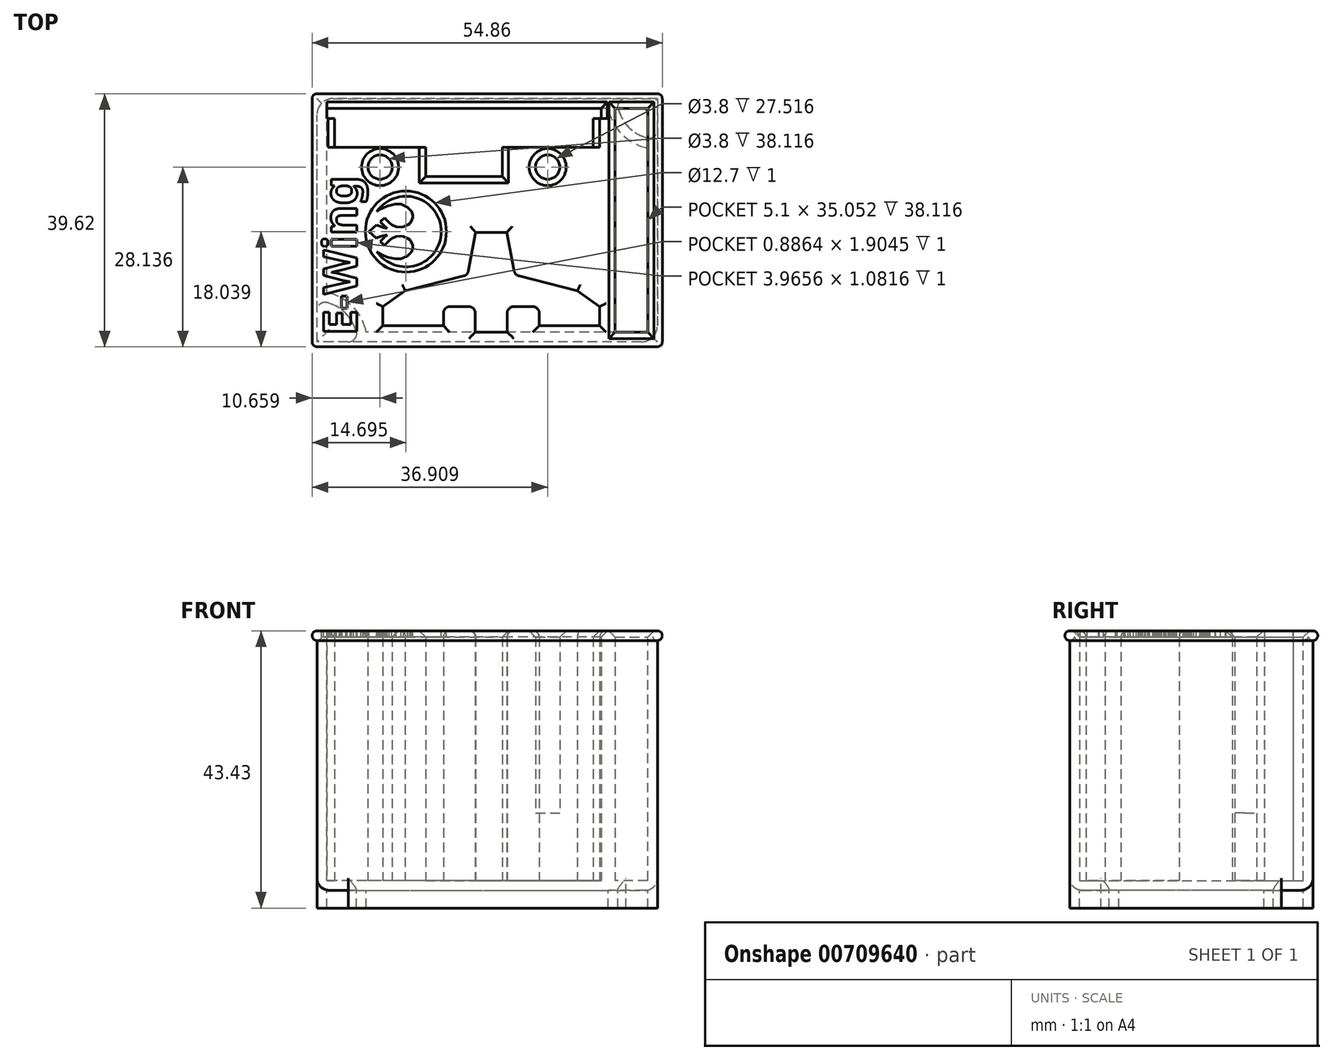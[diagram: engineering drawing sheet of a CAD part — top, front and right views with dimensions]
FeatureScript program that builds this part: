
annotation { "Feature Type Name" : "Feature", "Feature Type Description" : "" }
export const myFeature = defineFeature(function(context is Context, id is Id, definition is map)
    precondition{}
    {
        {
            var Q0;
            Q0=qCreatedBy(makeId("Front.planeOp"),FACE);
            var sketch = newSketch(context, id + "F0", { "sketchPlane" : qUnion([Q0])});
            skLineSegment(sketch, "E0.bottom", {"start": v(26.67, -20.32) * mm, "end": v(-26.67, -20.32) * mm});
            skLineSegment(sketch, "E0.top", {"start": v(26.67, 20.32) * mm, "end": v(-26.67, 20.32) * mm});
            skLineSegment(sketch, "E0.left", {"start": v(26.67, -20.32) * mm, "end": v(26.67, 20.32) * mm});
            skLineSegment(sketch, "E0.right", {"start": v(-26.67, -20.32) * mm, "end": v(-26.67, 20.32) * mm});
            skPoint(sketch, "E0.middle", {"position": v(0, 0) * mm});
            skSolve(sketch);
        }
        {
            var Q0;
            Q0=makeQuery(id+"F0.imprint","IMPRINT",FACE,{"disambiguationData":[TD([[makeQuery(id+"F0.imprint","IMPRINT",EDGE,{"derivedFrom":sQuery(id+"F0.wireOp",EDGE,"E0.bottom")}),-1.0]])]});
            extrude(context, id + "F1", {"entities" : qUnion([Q0]), "depth" : 38.1 * mm, "symmetric" : true});
        }
        {
            var Q0;
            Q0=makeQuery(id+"F1.opExtrude","SWEPT_FACE",FACE,{"disambiguationData":[OSD([sQuery(id+"F0.wireOp",EDGE,"E0.top")])]});
            shell(context, id + "F2", {"entities" : qUnion([Q0]), "thickness" : 1.52 * mm});
        }
        {
            var Q0;
            Q0=makeQuery(id+"F1.opExtrude","CAP_FACE",FACE,{"disambiguationData":[OSD([sQuery(id+"F0.wireOp",EDGE,"E0.bottom"),sQuery(id+"F0.wireOp",EDGE,"E0.top"),sQuery(id+"F0.wireOp",EDGE,"E0.left"),sQuery(id+"F0.wireOp",EDGE,"E0.right")])],"isStart":false});
            var sketch = newSketch(context, id + "F3", { "sketchPlane" : qUnion([Q0])});
            skArc(sketch, "E1", {"start": v(-26.67, 20.32) * mm, "mid": v(-27.43, 19.56) * mm, "end": v(-26.67, 18.8) * mm});
            skSolve(sketch);
        }
        {
            var Q0;
            {var subQ0=sQuery(id+"F3.wireOp",EDGE,"E1");Q0=makeQuery(id+"F3.imprint","IMPRINT",FACE,{"disambiguationData":[TD([[makeQuery(id+"F3.imprint","IMPRINT",EDGE,{"derivedFrom":subQ0}),1.0]])]});}
            var Q1;
            Q1=makeQuery(id+"F1.opExtrude","SWEPT_EDGE",EDGE,{"disambiguationData":[OSD([sQuery(id+"F0.wireOp",EDGE,"E0.top"),sQuery(id+"F0.wireOp",EDGE,"E0.right")])]});
            var Q2;
            Q2=makeQuery(id+"F1.opExtrude","CAP_EDGE",EDGE,{"disambiguationData":[OSD([sQuery(id+"F0.wireOp",EDGE,"E0.top")])],"isStart":true});
            var Q3;
            Q3=makeQuery(id+"F1.opExtrude","SWEPT_EDGE",EDGE,{"disambiguationData":[OSD([sQuery(id+"F0.wireOp",EDGE,"E0.top"),sQuery(id+"F0.wireOp",EDGE,"E0.left")])]});
            var Q4;
            Q4=makeQuery(id+"F1.opExtrude","CAP_EDGE",EDGE,{"disambiguationData":[OSD([sQuery(id+"F0.wireOp",EDGE,"E0.top")])],"isStart":false});
            sweep(context, id + "F4", {"operationType" : NewBodyOperationType.ADD, "profiles" : qUnion([Q0]), "path" : qUnion([Q1, Q2, Q3, Q4])});
        }
        {
            var Q0;
            Q0=makeQuery(id+"F1.opExtrude","SWEPT_FACE",FACE,{"disambiguationData":[OSD([sQuery(id+"F0.wireOp",EDGE,"E0.bottom")])]});
            var sketch = newSketch(context, id + "F5", { "sketchPlane" : qUnion([Q0])});
            skLineSegment(sketch, "E2.bottom", {"start": v(26.67, 19.05) * mm, "end": v(21.75, 19.05) * mm});
            skLineSegment(sketch, "E2.left", {"start": v(26.67, 19.05) * mm, "end": v(26.67, 14.13) * mm});
            skPoint(sketch, "E3.newPointA", {"position": v(20.32, 19.05) * mm});
            skArc(sketch, "E4", {"start": v(20.52, 17.46) * mm, "mid": v(22.18, 14.56) * mm, "end": v(25.08, 12.9) * mm});
            skArc(sketch, "E5.filletArc", {"start": v(21.75, 19.05) * mm, "mid": v(20.75, 18.56) * mm, "end": v(20.52, 17.46) * mm});
            skPoint(sketch, "E6.visualSharp", {"position": v(26.67, 12.7) * mm});
            skArc(sketch, "E6.filletArc", {"start": v(25.08, 12.9) * mm, "mid": v(26.18, 13.13) * mm, "end": v(26.67, 14.13) * mm});
            skArc(sketch, "E7.MirrorCS", {"start": v(-21.75, 19.05) * mm, "mid": v(-20.75, 18.56) * mm, "end": v(-20.52, 17.46) * mm});
            skArc(sketch, "E8.MirrorCS", {"start": v(-20.52, 17.46) * mm, "mid": v(-22.18, 14.56) * mm, "end": v(-25.08, 12.9) * mm});
            skArc(sketch, "E9.MirrorCS", {"start": v(-25.08, 12.9) * mm, "mid": v(-26.18, 13.13) * mm, "end": v(-26.67, 14.13) * mm});
            skLineSegment(sketch, "E10.MirrorCS", {"start": v(-26.67, 19.05) * mm, "end": v(-26.67, 14.13) * mm});
            skLineSegment(sketch, "E11.MirrorCS", {"start": v(-26.67, 19.05) * mm, "end": v(-21.75, 19.05) * mm});
            skArc(sketch, "E12.MirrorCS", {"start": v(-20.52, -17.46) * mm, "mid": v(-22.18, -14.56) * mm, "end": v(-25.08, -12.9) * mm});
            skArc(sketch, "E13.MirrorCS", {"start": v(-21.75, -19.05) * mm, "mid": v(-20.75, -18.56) * mm, "end": v(-20.52, -17.46) * mm});
            skLineSegment(sketch, "E14.MirrorCS", {"start": v(-26.67, -19.05) * mm, "end": v(-21.75, -19.05) * mm});
            skLineSegment(sketch, "E15.MirrorCS", {"start": v(-26.67, -19.05) * mm, "end": v(-26.67, -14.13) * mm});
            skArc(sketch, "E16.MirrorCS", {"start": v(-25.08, -12.9) * mm, "mid": v(-26.18, -13.13) * mm, "end": v(-26.67, -14.13) * mm});
            skArc(sketch, "E17.MirrorCS", {"start": v(21.75, -19.05) * mm, "mid": v(20.75, -18.56) * mm, "end": v(20.52, -17.46) * mm});
            skArc(sketch, "E18.MirrorCS", {"start": v(20.52, -17.46) * mm, "mid": v(22.18, -14.56) * mm, "end": v(25.08, -12.9) * mm});
            skArc(sketch, "E19.MirrorCS", {"start": v(25.08, -12.9) * mm, "mid": v(26.18, -13.13) * mm, "end": v(26.67, -14.13) * mm});
            skLineSegment(sketch, "E20.MirrorCS", {"start": v(26.67, -19.05) * mm, "end": v(26.67, -14.13) * mm});
            skLineSegment(sketch, "E21.MirrorCS", {"start": v(26.67, -19.05) * mm, "end": v(21.75, -19.05) * mm});
            skSolve(sketch);
        }
        {
            var Q0;
            Q0=makeQuery(id+"F5.imprint","IMPRINT",FACE,{"disambiguationData":[TD([[makeQuery(id+"F5.imprint","IMPRINT",EDGE,{"derivedFrom":sQuery(id+"F5.wireOp",EDGE,"E2.bottom")}),1.0]])]});
            var Q1;
            Q1=makeQuery(id+"F5.imprint","IMPRINT",FACE,{"disambiguationData":[TD([[makeQuery(id+"F5.imprint","IMPRINT",EDGE,{"derivedFrom":sQuery(id+"F5.wireOp",EDGE,"E8.MirrorCS")}),-1.0]])]});
            var Q2;
            Q2=makeQuery(id+"F5.imprint","IMPRINT",FACE,{"disambiguationData":[TD([[makeQuery(id+"F5.imprint","IMPRINT",EDGE,{"derivedFrom":sQuery(id+"F5.wireOp",EDGE,"E12.MirrorCS")}),1.0]])]});
            var Q3;
            Q3=makeQuery(id+"F5.imprint","IMPRINT",FACE,{"disambiguationData":[TD([[makeQuery(id+"F5.imprint","IMPRINT",EDGE,{"derivedFrom":sQuery(id+"F5.wireOp",EDGE,"E17.MirrorCS")}),-1.0]])]});
            extrude(context, id + "F6", {"entities" : qUnion([Q0, Q1, Q2, Q3]), "operationType" : NewBodyOperationType.ADD, "depth" : 2.8 * mm});
        }
        {
            var Q0;
            Q0=makeQuery(id+"F6.opExtrude","CAP_FACE",FACE,{"disambiguationData":[OSD([sQuery(id+"F5.wireOp",EDGE,"E2.bottom"),sQuery(id+"F5.wireOp",EDGE,"E2.left"),sQuery(id+"F5.wireOp",EDGE,"E4"),sQuery(id+"F5.wireOp",EDGE,"E5.filletArc"),sQuery(id+"F5.wireOp",EDGE,"E6.filletArc")])],"isStart":false});
            var Q1;
            Q1=makeQuery(id+"F6.opExtrude","CAP_FACE",FACE,{"disambiguationData":[OSD([sQuery(id+"F5.wireOp",EDGE,"E8.MirrorCS"),sQuery(id+"F5.wireOp",EDGE,"E9.MirrorCS"),sQuery(id+"F5.wireOp",EDGE,"E10.MirrorCS"),sQuery(id+"F5.wireOp",EDGE,"E7.MirrorCS"),sQuery(id+"F5.wireOp",EDGE,"E11.MirrorCS")])],"isStart":false});
            var Q2;
            Q2=makeQuery(id+"F6.opExtrude","CAP_FACE",FACE,{"disambiguationData":[OSD([sQuery(id+"F5.wireOp",EDGE,"E12.MirrorCS"),sQuery(id+"F5.wireOp",EDGE,"E13.MirrorCS"),sQuery(id+"F5.wireOp",EDGE,"E14.MirrorCS"),sQuery(id+"F5.wireOp",EDGE,"E15.MirrorCS"),sQuery(id+"F5.wireOp",EDGE,"E16.MirrorCS")])],"isStart":false});
            var Q3;
            Q3=makeQuery(id+"F6.opExtrude","CAP_FACE",FACE,{"disambiguationData":[OSD([sQuery(id+"F5.wireOp",EDGE,"E17.MirrorCS"),sQuery(id+"F5.wireOp",EDGE,"E18.MirrorCS"),sQuery(id+"F5.wireOp",EDGE,"E19.MirrorCS"),sQuery(id+"F5.wireOp",EDGE,"E20.MirrorCS"),sQuery(id+"F5.wireOp",EDGE,"E21.MirrorCS")])],"isStart":false});
            shell(context, id + "F7", {"entities" : qUnion([Q0, Q1, Q2, Q3]), "thickness" : 1.52 * mm});
        }
        {
            var Q0;
            Q0=makeQuery(id+"F1.opExtrude","SWEPT_EDGE",EDGE,{"disambiguationData":[OSD([sQuery(id+"F0.wireOp",EDGE,"E0.bottom"),sQuery(id+"F0.wireOp",EDGE,"E0.right")])]});
            var Q1;
            Q1=makeQuery(id+"F1.opExtrude","CAP_EDGE",EDGE,{"disambiguationData":[OSD([sQuery(id+"F0.wireOp",EDGE,"E0.bottom")])],"isStart":false});
            var Q2;
            Q2=makeQuery(id+"F1.opExtrude","SWEPT_EDGE",EDGE,{"disambiguationData":[OSD([sQuery(id+"F0.wireOp",EDGE,"E0.bottom"),sQuery(id+"F0.wireOp",EDGE,"E0.left")])]});
            var Q3;
            Q3=makeQuery(id+"F1.opExtrude","CAP_EDGE",EDGE,{"disambiguationData":[OSD([sQuery(id+"F0.wireOp",EDGE,"E0.bottom")])],"isStart":true});
            fillet(context, id + "F8", {"entities" : qUnion([Q0, Q1, Q2, Q3]), "radius" : 1.9 * mm, "tangentPropagation" : true, "allowEdgeOverflow" : false});
        }
        {
            var Q0;
            Q0=makeQuery(id+"F4.opSweep","MID_CAP_EDGE",EDGE,{"disambiguationData":[OSD([sQuery(id+"F0.wireOp",EDGE,"E0.top"),sQuery(id+"F0.wireOp",EDGE,"E0.left"),sQuery(id+"F3.wireOp",EDGE,"E1")])],"capPos":3.0});
            var Q1;
            Q1=makeQuery(id+"F4.opSweep","MID_CAP_EDGE",EDGE,{"disambiguationData":[OSD([sQuery(id+"F0.wireOp",EDGE,"E0.top"),sQuery(id+"F0.wireOp",EDGE,"E0.left"),sQuery(id+"F3.wireOp",EDGE,"E1")])],"capPos":2.0});
            var Q2;
            Q2=makeQuery(id+"F4.opSweep","MID_CAP_EDGE",EDGE,{"disambiguationData":[OSD([sQuery(id+"F0.wireOp",EDGE,"E0.top"),sQuery(id+"F0.wireOp",EDGE,"E0.right"),sQuery(id+"F3.wireOp",EDGE,"E1")])],"capPos":1.0});
            var Q3;
            Q3=makeQuery(id+"F4.opSweep","CAP_EDGE",EDGE,{"disambiguationData":[OSD([sQuery(id+"F0.wireOp",EDGE,"E0.top"),sQuery(id+"F0.wireOp",EDGE,"E0.right"),sQuery(id+"F3.wireOp",EDGE,"E1")])],"isStart":true});
            fillet(context, id + "F9", {"entities" : qUnion([Q0, Q1, Q2, Q3]), "radius" : 0.76 * mm, "tangentPropagation" : true, "allowEdgeOverflow" : false});
        }
        {
            var Q0;
            Q0=makeQuery(id+"F6.boolean.opBoolean","MERGE",EDGE,{"derivedFrom":[makeQuery(id+"F1.opExtrude","CAP_EDGE",EDGE,{"disambiguationData":[OSD([sQuery(id+"F0.wireOp",EDGE,"E0.left")])],"isStart":false}),makeQuery(id+"F6.opExtrude","SWEPT_EDGE",EDGE,{"disambiguationData":[OSD([sQuery(id+"F5.wireOp",EDGE,"E2.bottom"),sQuery(id+"F5.wireOp",EDGE,"E2.left")])]})]});
            var Q1;
            Q1=makeQuery(id+"F6.boolean.opBoolean","MERGE",EDGE,{"derivedFrom":[makeQuery(id+"F1.opExtrude","CAP_EDGE",EDGE,{"disambiguationData":[OSD([sQuery(id+"F0.wireOp",EDGE,"E0.left")])],"isStart":true}),makeQuery(id+"F6.opExtrude","SWEPT_EDGE",EDGE,{"disambiguationData":[OSD([sQuery(id+"F5.wireOp",EDGE,"E20.MirrorCS"),sQuery(id+"F5.wireOp",EDGE,"E21.MirrorCS")])]})]});
            var Q2;
            Q2=makeQuery(id+"F6.boolean.opBoolean","MERGE",EDGE,{"derivedFrom":[makeQuery(id+"F1.opExtrude","CAP_EDGE",EDGE,{"disambiguationData":[OSD([sQuery(id+"F0.wireOp",EDGE,"E0.right")])],"isStart":false}),makeQuery(id+"F6.opExtrude","SWEPT_EDGE",EDGE,{"disambiguationData":[OSD([sQuery(id+"F5.wireOp",EDGE,"E10.MirrorCS"),sQuery(id+"F5.wireOp",EDGE,"E11.MirrorCS")])]})]});
            var Q3;
            Q3=makeQuery(id+"F6.boolean.opBoolean","MERGE",EDGE,{"derivedFrom":[makeQuery(id+"F1.opExtrude","CAP_EDGE",EDGE,{"disambiguationData":[OSD([sQuery(id+"F0.wireOp",EDGE,"E0.right")])],"isStart":true}),makeQuery(id+"F6.opExtrude","SWEPT_EDGE",EDGE,{"disambiguationData":[OSD([sQuery(id+"F5.wireOp",EDGE,"E14.MirrorCS"),sQuery(id+"F5.wireOp",EDGE,"E15.MirrorCS")])]})]});
            fillet(context, id + "F10", {"entities" : qUnion([Q0, Q1, Q2, Q3]), "radius" : 2.54 * mm, "tangentPropagation" : true, "allowEdgeOverflow" : false});
        }
        {
            var Q0;
            Q0=makeQuery(id+"F2.opShell","OFFSET_FACE",FACE,{"disambiguationData":[OSD([sQuery(id+"F0.wireOp",EDGE,"E0.bottom")])]});
            var sketch = newSketch(context, id + "F11", { "sketchPlane" : qUnion([Q0])});
            skLineSegment(sketch, "E22.bottom", {"start": v(-51.93, -9.02) * mm, "end": v(-66.18, -9.02) * mm});
            skLineSegment(sketch, "E22.top", {"start": v(-51.93, -2.92) * mm, "end": v(-92.43, -2.92) * mm});
            skLineSegment(sketch, "E22.left", {"start": v(-51.93, -9.02) * mm, "end": v(-51.93, -4.52) * mm});
            skLineSegment(sketch, "E22.right", {"start": v(-92.43, -9.02) * mm, "end": v(-92.43, -4.52) * mm});
            skPoint(sketch, "E22.middle", {"position": v(-72.18, -5.97) * mm});
            skLineSegment(sketch, "E23.bottom", {"start": v(-93.68, -2.92) * mm, "end": v(-50.68, -2.92) * mm});
            skLineSegment(sketch, "E23.top", {"start": v(-93.68, -4.52) * mm, "end": v(-92.43, -4.52) * mm});
            skLineSegment(sketch, "E23.left", {"start": v(-93.68, -2.92) * mm, "end": v(-93.68, -4.52) * mm});
            skLineSegment(sketch, "E23.right", {"start": v(-50.68, -2.92) * mm, "end": v(-50.68, -4.52) * mm});
            skLineSegment(sketch, "E24.top", {"start": v(-78.18, -13.62) * mm, "end": v(-66.18, -13.62) * mm});
            skLineSegment(sketch, "E24.left", {"start": v(-78.18, -9.02) * mm, "end": v(-78.18, -13.62) * mm});
            skLineSegment(sketch, "E24.right", {"start": v(-66.18, -9.02) * mm, "end": v(-66.18, -13.62) * mm});
            skLineSegment(sketch, "E25.trimOffspring", {"start": v(-51.93, -4.52) * mm, "end": v(-50.68, -4.52) * mm});
            skLineSegment(sketch, "E26.trimOffspring", {"start": v(-78.18, -9.02) * mm, "end": v(-92.43, -9.02) * mm});
            skCircle(sketch, "E27", {"center": v(-59.06, -12.12) * mm, "radius": 1.9 * mm});
            skLineSegment(sketch, "E28", {"start": v(-59.06, -9.02) * mm, "end": v(-59.06, -10.22) * mm, "construction": true});
            skPoint(sketch, "E29.startSnap0", {"position": v(-72.18, -2.92) * mm});
            skLineSegment(sketch, "E30.MirrorCS", {"start": v(-85.3, -9.02) * mm, "end": v(-85.3, -10.22) * mm, "construction": true});
            skCircle(sketch, "E31.MirrorC", {"center": v(-85.3, -12.12) * mm, "radius": 1.9 * mm});
            skLineSegment(sketch, "E32.bottom", {"start": v(16.6, 11.43) * mm, "end": v(2.35, 11.43) * mm});
            skLineSegment(sketch, "E32.top", {"start": v(16.6, 17.53) * mm, "end": v(-23.9, 17.53) * mm});
            skLineSegment(sketch, "E32.left", {"start": v(16.6, 11.43) * mm, "end": v(16.6, 15.93) * mm});
            skLineSegment(sketch, "E32.right", {"start": v(-23.9, 11.43) * mm, "end": v(-23.9, 15.93) * mm});
            skPoint(sketch, "E32.middle", {"position": v(-3.65, 14.48) * mm});
            skLineSegment(sketch, "E33.bottom", {"start": v(-25.15, 17.53) * mm, "end": v(17.85, 17.53) * mm});
            skLineSegment(sketch, "E33.top", {"start": v(-25.15, 15.93) * mm, "end": v(-23.9, 15.93) * mm});
            skLineSegment(sketch, "E33.left", {"start": v(-25.15, 17.53) * mm, "end": v(-25.15, 15.93) * mm});
            skLineSegment(sketch, "E33.right", {"start": v(17.85, 17.53) * mm, "end": v(17.85, 15.93) * mm});
            skLineSegment(sketch, "E34.top", {"start": v(-9.65, 6.83) * mm, "end": v(2.35, 6.83) * mm});
            skLineSegment(sketch, "E34.left", {"start": v(-9.65, 11.43) * mm, "end": v(-9.65, 6.83) * mm});
            skLineSegment(sketch, "E34.right", {"start": v(2.35, 11.43) * mm, "end": v(2.35, 6.83) * mm});
            skLineSegment(sketch, "E35.trimOffspring", {"start": v(16.6, 15.93) * mm, "end": v(17.85, 15.93) * mm});
            skLineSegment(sketch, "E36.trimOffspring", {"start": v(-9.65, 11.43) * mm, "end": v(-23.9, 11.43) * mm});
            skCircle(sketch, "E37", {"center": v(9.48, 8.33) * mm, "radius": 1.9 * mm});
            skLineSegment(sketch, "E38", {"start": v(9.48, 11.43) * mm, "end": v(9.48, 10.23) * mm, "construction": true});
            skPoint(sketch, "E39.startSnap0", {"position": v(-3.65, 17.53) * mm});
            skLineSegment(sketch, "E40.MirrorCS", {"start": v(-16.77, 11.43) * mm, "end": v(-16.77, 10.23) * mm, "construction": true});
            skCircle(sketch, "E41.MirrorC", {"center": v(-16.77, 8.33) * mm, "radius": 1.9 * mm});
            skSolve(sketch);
        }
        {
            var Q0;
            Q0=makeQuery(id+"F2.opShell","OFFSET_FACE",FACE,{"disambiguationData":[OSD([sQuery(id+"F0.wireOp",EDGE,"E0.bottom")])]});
            var sketch = newSketch(context, id + "F12", { "sketchPlane" : qUnion([Q0])});
            skLineSegment(sketch, "E42.bottom", {"start": v(20.05, -17.7) * mm, "end": v(20.05, 17.7) * mm});
            skLineSegment(sketch, "E42.top", {"start": v(25.15, -17.7) * mm, "end": v(25.15, 17.7) * mm});
            skLineSegment(sketch, "E42.left", {"start": v(20.05, -17.7) * mm, "end": v(25.15, -17.7) * mm});
            skLineSegment(sketch, "E42.right", {"start": v(20.05, 17.7) * mm, "end": v(25.15, 17.7) * mm});
            skPoint(sketch, "E42.middle", {"position": v(22.6, 0) * mm});
            skSolve(sketch);
        }
        {
            var Q0;
            Q0=makeQuery(id+"F2.opShell","OFFSET_FACE",FACE,{"disambiguationData":[OSD([sQuery(id+"F0.wireOp",EDGE,"E0.bottom")])]});
            var sketch = newSketch(context, id + "F13", { "sketchPlane" : qUnion([Q0])});
            skLineSegment(sketch, "E43", {"start": v(-1.2, -17.53) * mm, "end": v(-3.65, -17.53) * mm});
            skLineSegment(sketch, "E44.MirrorCS", {"start": v(-6.1, -17.53) * mm, "end": v(-3.65, -17.53) * mm});
            skLineSegment(sketch, "E45", {"start": v(-1.15, -17.53) * mm, "end": v(-1.15, -13.53) * mm});
            skLineSegment(sketch, "E46", {"start": v(-1.15, -13.53) * mm, "end": v(3.85, -13.53) * mm});
            skLineSegment(sketch, "E47", {"start": v(3.85, -13.53) * mm, "end": v(3.85, -16.53) * mm});
            skPoint(sketch, "E48.visualSharp", {"position": v(3.85, -13.53) * mm});
            skPoint(sketch, "E49.visualSharp", {"position": v(-1.15, -13.53) * mm});
            skLineSegment(sketch, "E50", {"start": v(-1.15, -17.53) * mm, "end": v(-3.65, -17.53) * mm});
            skLineSegment(sketch, "E51", {"start": v(-1.2, -1.93) * mm, "end": v(-3.65, -1.93) * mm});
            skLineSegment(sketch, "E52", {"start": v(13.35, -16.53) * mm, "end": v(13.35, -13.53) * mm});
            skLineSegment(sketch, "E53", {"start": v(0.05, -8.58) * mm, "end": v(9.85, -11.03) * mm});
            skLineSegment(sketch, "E54", {"start": v(9.85, -11.03) * mm, "end": v(13.35, -13.53) * mm});
            skLineSegment(sketch, "E55", {"start": v(3.85, -16.53) * mm, "end": v(13.35, -16.53) * mm});
            skLineSegment(sketch, "E56", {"start": v(-1.2, -1.93) * mm, "end": v(0.05, -8.58) * mm});
            skLineSegment(sketch, "E57.MirrorCS", {"start": v(-6.1, -1.93) * mm, "end": v(-3.65, -1.93) * mm});
            skLineSegment(sketch, "E58.MirrorCS", {"start": v(-11.15, -13.53) * mm, "end": v(-11.15, -16.53) * mm});
            skLineSegment(sketch, "E59.MirrorCS", {"start": v(-6.15, -13.53) * mm, "end": v(-11.15, -13.53) * mm});
            skLineSegment(sketch, "E60.MirrorCS", {"start": v(-6.15, -17.53) * mm, "end": v(-3.65, -17.53) * mm});
            skLineSegment(sketch, "E61.MirrorCS", {"start": v(-11.15, -16.53) * mm, "end": v(-20.65, -16.53) * mm});
            skLineSegment(sketch, "E62.MirrorCS", {"start": v(-6.15, -17.53) * mm, "end": v(-6.15, -13.53) * mm});
            skPoint(sketch, "E63.MirrorP", {"position": v(-6.15, -13.53) * mm});
            skPoint(sketch, "E64.MirrorP", {"position": v(-11.15, -13.53) * mm});
            skLineSegment(sketch, "E65.MirrorCS", {"start": v(-20.65, -16.53) * mm, "end": v(-20.65, -13.53) * mm});
            skLineSegment(sketch, "E66.MirrorCS", {"start": v(-7.34, -8.58) * mm, "end": v(-17.15, -11.03) * mm});
            skLineSegment(sketch, "E67.MirrorCS", {"start": v(-6.1, -1.93) * mm, "end": v(-7.34, -8.58) * mm});
            skLineSegment(sketch, "E68.MirrorCS", {"start": v(-17.15, -11.03) * mm, "end": v(-20.65, -13.53) * mm});
            skPoint(sketch, "E69.0", {"position": v(-3.65, 6.83) * mm});
            skSolve(sketch);
        }
        {
            var Q0;
            Q0=makeQuery(id+"F2.opShell","OFFSET_FACE",FACE,{"disambiguationData":[OSD([sQuery(id+"F0.wireOp",EDGE,"E0.bottom")])]});
            var sketch = newSketch(context, id + "F14", { "sketchPlane" : qUnion([Q0])});
            skLineSegment(sketch, "E70.0", {"start": v(3.1, -17.53) * mm, "end": v(0.65, -17.53) * mm});
            skLineSegment(sketch, "E70.1", {"start": v(-1.8, -17.53) * mm, "end": v(0.65, -17.53) * mm});
            skLineSegment(sketch, "E70.2", {"start": v(3.15, -17.53) * mm, "end": v(3.15, -13.53) * mm});
            skLineSegment(sketch, "E70.3", {"start": v(3.15, -13.53) * mm, "end": v(8.15, -13.53) * mm});
            skLineSegment(sketch, "E70.4", {"start": v(8.15, -13.53) * mm, "end": v(8.15, -16.53) * mm});
            skPoint(sketch, "E70.5", {"position": v(8.15, -13.53) * mm});
            skPoint(sketch, "E70.6", {"position": v(3.15, -13.53) * mm});
            skLineSegment(sketch, "E70.7", {"start": v(3.15, -17.53) * mm, "end": v(0.65, -17.53) * mm});
            skLineSegment(sketch, "E70.8", {"start": v(3.1, -1.93) * mm, "end": v(0.65, -1.93) * mm});
            skLineSegment(sketch, "E70.9", {"start": v(17.65, -16.53) * mm, "end": v(17.65, -13.53) * mm});
            skLineSegment(sketch, "E70.10", {"start": v(4.34, -8.58) * mm, "end": v(14.15, -11.03) * mm});
            skLineSegment(sketch, "E70.11", {"start": v(14.15, -11.03) * mm, "end": v(17.65, -13.53) * mm});
            skLineSegment(sketch, "E70.12", {"start": v(8.15, -16.53) * mm, "end": v(17.65, -16.53) * mm});
            skLineSegment(sketch, "E70.13", {"start": v(3.1, -1.93) * mm, "end": v(4.34, -8.58) * mm});
            skLineSegment(sketch, "E70.14", {"start": v(-1.8, -1.93) * mm, "end": v(0.65, -1.93) * mm});
            skLineSegment(sketch, "E70.15", {"start": v(-6.85, -13.53) * mm, "end": v(-6.85, -16.53) * mm});
            skLineSegment(sketch, "E70.16", {"start": v(-1.85, -13.53) * mm, "end": v(-6.85, -13.53) * mm});
            skLineSegment(sketch, "E70.17", {"start": v(-1.85, -17.53) * mm, "end": v(0.65, -17.53) * mm});
            skLineSegment(sketch, "E70.18", {"start": v(-6.85, -16.53) * mm, "end": v(-16.35, -16.53) * mm});
            skLineSegment(sketch, "E70.19", {"start": v(-1.85, -17.53) * mm, "end": v(-1.85, -13.53) * mm});
            skPoint(sketch, "E70.20", {"position": v(-1.85, -13.53) * mm});
            skPoint(sketch, "E70.21", {"position": v(-6.85, -13.53) * mm});
            skLineSegment(sketch, "E70.22", {"start": v(-16.35, -16.53) * mm, "end": v(-16.35, -13.53) * mm});
            skLineSegment(sketch, "E70.23", {"start": v(-3.05, -8.58) * mm, "end": v(-12.85, -11.03) * mm});
            skLineSegment(sketch, "E70.24", {"start": v(-1.8, -1.93) * mm, "end": v(-3.05, -8.58) * mm});
            skLineSegment(sketch, "E70.25", {"start": v(-12.85, -11.03) * mm, "end": v(-16.35, -13.53) * mm});
            skPoint(sketch, "E70.26", {"position": v(-3.65, 6.83) * mm});
            skLineSegment(sketch, "E71.0", {"start": v(20.05, -17.7) * mm, "end": v(20.05, 17.7) * mm});
            skLineSegment(sketch, "E71.1", {"start": v(25.15, -17.7) * mm, "end": v(25.15, 17.7) * mm});
            skLineSegment(sketch, "E71.2", {"start": v(20.05, -17.7) * mm, "end": v(25.15, -17.7) * mm});
            skLineSegment(sketch, "E71.3", {"start": v(20.05, 17.7) * mm, "end": v(25.15, 17.7) * mm});
            skPoint(sketch, "E71.4", {"position": v(22.6, 0) * mm});
            skLineSegment(sketch, "E71.5", {"start": v(-51.93, -9.02) * mm, "end": v(-66.18, -9.02) * mm});
            skLineSegment(sketch, "E71.6", {"start": v(-51.93, -2.92) * mm, "end": v(-92.43, -2.92) * mm});
            skLineSegment(sketch, "E71.7", {"start": v(-51.93, -9.02) * mm, "end": v(-51.93, -4.52) * mm});
            skLineSegment(sketch, "E71.8", {"start": v(-92.43, -9.02) * mm, "end": v(-92.43, -4.52) * mm});
            skPoint(sketch, "E71.9", {"position": v(-72.18, -5.97) * mm});
            skLineSegment(sketch, "E71.10", {"start": v(-93.68, -2.92) * mm, "end": v(-50.68, -2.92) * mm});
            skLineSegment(sketch, "E71.11", {"start": v(-93.68, -4.52) * mm, "end": v(-92.43, -4.52) * mm});
            skLineSegment(sketch, "E71.12", {"start": v(-93.68, -2.92) * mm, "end": v(-93.68, -4.52) * mm});
            skLineSegment(sketch, "E71.13", {"start": v(-50.68, -2.92) * mm, "end": v(-50.68, -4.52) * mm});
            skLineSegment(sketch, "E71.14", {"start": v(-78.18, -13.62) * mm, "end": v(-66.18, -13.62) * mm});
            skLineSegment(sketch, "E71.15", {"start": v(-78.18, -9.02) * mm, "end": v(-78.18, -13.62) * mm});
            skLineSegment(sketch, "E71.16", {"start": v(-66.18, -9.02) * mm, "end": v(-66.18, -13.62) * mm});
            skLineSegment(sketch, "E71.17", {"start": v(-51.93, -4.52) * mm, "end": v(-50.68, -4.52) * mm});
            skLineSegment(sketch, "E71.18", {"start": v(-78.18, -9.02) * mm, "end": v(-92.43, -9.02) * mm});
            skCircle(sketch, "E71.19", {"center": v(-59.06, -12.12) * mm, "radius": 1.9 * mm});
            skLineSegment(sketch, "E71.20", {"start": v(-59.06, -9.02) * mm, "end": v(-59.06, -10.22) * mm});
            skPoint(sketch, "E71.21", {"position": v(-72.18, -2.92) * mm});
            skLineSegment(sketch, "E71.22", {"start": v(-85.3, -9.02) * mm, "end": v(-85.3, -10.22) * mm});
            skCircle(sketch, "E71.23", {"center": v(-85.3, -12.12) * mm, "radius": 1.9 * mm});
            skLineSegment(sketch, "E71.24", {"start": v(16.6, 11.43) * mm, "end": v(2.35, 11.43) * mm});
            skLineSegment(sketch, "E71.25", {"start": v(16.6, 17.53) * mm, "end": v(-23.9, 17.53) * mm});
            skLineSegment(sketch, "E71.26", {"start": v(16.6, 11.43) * mm, "end": v(16.6, 15.93) * mm});
            skLineSegment(sketch, "E71.27", {"start": v(-23.9, 11.43) * mm, "end": v(-23.9, 15.93) * mm});
            skPoint(sketch, "E71.28", {"position": v(-3.65, 14.48) * mm});
            skLineSegment(sketch, "E71.29", {"start": v(-25.15, 17.53) * mm, "end": v(17.85, 17.53) * mm});
            skLineSegment(sketch, "E71.30", {"start": v(-25.15, 15.93) * mm, "end": v(-23.9, 15.93) * mm});
            skLineSegment(sketch, "E71.31", {"start": v(-25.15, 17.53) * mm, "end": v(-25.15, 15.93) * mm});
            skLineSegment(sketch, "E71.32", {"start": v(17.85, 17.53) * mm, "end": v(17.85, 15.93) * mm});
            skLineSegment(sketch, "E71.33", {"start": v(-9.65, 6.83) * mm, "end": v(2.35, 6.83) * mm});
            skLineSegment(sketch, "E71.34", {"start": v(-9.65, 11.43) * mm, "end": v(-9.65, 6.83) * mm});
            skLineSegment(sketch, "E71.35", {"start": v(2.35, 11.43) * mm, "end": v(2.35, 6.83) * mm});
            skLineSegment(sketch, "E71.36", {"start": v(16.6, 15.93) * mm, "end": v(17.85, 15.93) * mm});
            skLineSegment(sketch, "E71.37", {"start": v(-9.65, 11.43) * mm, "end": v(-23.9, 11.43) * mm});
            skCircle(sketch, "E71.38", {"center": v(9.48, 8.33) * mm, "radius": 1.9 * mm});
            skLineSegment(sketch, "E71.39", {"start": v(9.48, 11.43) * mm, "end": v(9.48, 10.23) * mm});
            skPoint(sketch, "E71.40", {"position": v(-3.65, 17.53) * mm});
            skLineSegment(sketch, "E71.41", {"start": v(-16.77, 11.43) * mm, "end": v(-16.77, 10.23) * mm});
            skCircle(sketch, "E71.42", {"center": v(-16.77, 8.33) * mm, "radius": 1.9 * mm});
            skLineSegment(sketch, "E72", {"start": v(17.65, -16.53) * mm, "end": v(20.05, -16.53) * mm, "construction": true});
            skSolve(sketch);
        }
        {
            var Q0;
            Q0=makeQuery(id+"F14.imprint","IMPRINT",FACE,{"disambiguationData":[TD([[makeQuery(id+"F14.imprint","IMPRINT",EDGE,{"derivedFrom":sQuery(id+"F14.wireOp",EDGE,"E71.42")}),-1.0]])]});
            var Q1;
            Q1=makeQuery(id+"F14.imprint","IMPRINT",FACE,{"disambiguationData":[TD([[makeQuery(id+"F14.imprint","IMPRINT",EDGE,{"derivedFrom":sQuery(id+"F14.wireOp",EDGE,"E71.38")}),1.0]])]});
            extrude(context, id + "F15", {"entities" : qUnion([Q0, Q1]), "operationType" : NewBodyOperationType.ADD, "depth" : 10.6 * mm, "offsetDistance" : 25 * mm});
        }
        {
            var Q0;
            {var subQ19=sQuery(id+"F14.wireOp",EDGE,"E70.2");Q0=makeQuery(id+"F14.imprint","IMPRINT",FACE,{"disambiguationData":[TD([[makeQuery(id+"F14.imprint","IMPRINT",EDGE,{"derivedFrom":subQ19}),-1.0]])]});}
            var Q1;
            {var subQ0=sQuery(id+"F0.wireOp",EDGE,"E0.right");var subQ1=sQuery(id+"F0.wireOp",EDGE,"E0.top");Q1=makeQuery(id+"F2.opShell","OFFSET_VERTEX",VERTEX,{"disambiguationData":[OSD([subQ1,subQ0]),TDD([makeQuery(id+"F1.opExtrude","CAP_VERTEX",VERTEX,{"disambiguationData":[OSD([subQ1,subQ0])],"isStart":true})])]});}
            extrude(context, id + "F16", {"entities" : qUnion([Q0]), "operationType" : NewBodyOperationType.ADD, "endBound" : BoundingType.UP_TO_VERTEX, "depth" : 36.12 * mm, "endBoundEntityVertex" : qUnion([Q1]), "offsetDistance" : 25 * mm});
        }
        {
            var Q0;
            Q0=makeQuery(id+"F16.opExtrude","CAP_EDGE",EDGE,{"disambiguationData":[OSD([sQuery(id+"F14.wireOp",EDGE,"E71.38")])],"isStart":false});
            var Q1;
            Q1=makeQuery(id+"F16.opExtrude","CAP_EDGE",EDGE,{"disambiguationData":[OSD([sQuery(id+"F14.wireOp",EDGE,"E71.42")])],"isStart":false});
            chamfer(context, id + "F17", {"entities" : qUnion([Q0, Q1]), "width" : 1 * mm, "tangentPropagation" : true});
        }
        {
            var Q0;
            Q0=makeQuery(id+"F16.opExtrude","CAP_EDGE",EDGE,{"disambiguationData":[OSD([sQuery(id+"F14.wireOp",EDGE,"E71.34")])],"isStart":false});
            var Q1;
            Q1=makeQuery(id+"F16.opExtrude","CAP_EDGE",EDGE,{"disambiguationData":[OSD([sQuery(id+"F14.wireOp",EDGE,"E71.33")])],"isStart":false});
            var Q2;
            Q2=makeQuery(id+"F16.opExtrude","CAP_EDGE",EDGE,{"disambiguationData":[OSD([sQuery(id+"F14.wireOp",EDGE,"E71.35")])],"isStart":false});
            var Q3;
            Q3=makeQuery(id+"F16.opExtrude","CAP_EDGE",EDGE,{"disambiguationData":[OSD([sQuery(id+"F14.wireOp",EDGE,"E71.26")])],"isStart":false});
            var Q4;
            Q4=makeQuery(id+"F16.opExtrude","CAP_EDGE",EDGE,{"disambiguationData":[OSD([sQuery(id+"F14.wireOp",EDGE,"E71.27")])],"isStart":false});
            var Q5;
            Q5=makeQuery(id+"F16.opExtrude","CAP_EDGE",EDGE,{"disambiguationData":[OSD([sQuery(id+"F14.wireOp",EDGE,"E71.32")])],"isStart":false});
            var Q6;
            Q6=makeQuery(id+"F16.opExtrude","CAP_EDGE",EDGE,{"disambiguationData":[OSD([sQuery(id+"F14.wireOp",EDGE,"E71.0")])],"isStart":false});
            var Q7;
            {var subQ0=sQuery(id+"F0.wireOp",EDGE,"E0.right");var subQ4=sQuery(id+"F0.wireOp",EDGE,"E0.top");Q7=makeQuery(id+"F16.boolean.opBoolean","SPLIT",EDGE,{"disambiguationData":[TD([makeQuery(id+"F2.opShell","OFFSET_FACE",FACE,{"disambiguationData":[OSD([subQ0])]})])],"derivedFrom":makeQuery(id+"F2.opShell","OFFSET_EDGE",EDGE,{"disambiguationData":[OSD([subQ4]),TDD([makeQuery(id+"F1.opExtrude","CAP_EDGE",EDGE,{"disambiguationData":[OSD([subQ4])],"isStart":true})])]})});}
            var Q8;
            Q8=makeQuery(id+"F2.opShell","OFFSET_EDGE",EDGE,{"disambiguationData":[OSD([sQuery(id+"F0.wireOp",EDGE,"E0.top"),sQuery(id+"F0.wireOp",EDGE,"E0.left")])]});
            var Q9;
            {var subQ0=sQuery(id+"F0.wireOp",EDGE,"E0.left");var subQ4=sQuery(id+"F0.wireOp",EDGE,"E0.top");Q9=makeQuery(id+"F16.boolean.opBoolean","SPLIT",EDGE,{"disambiguationData":[TD([makeQuery(id+"F2.opShell","OFFSET_FACE",FACE,{"disambiguationData":[OSD([subQ0])]})])],"derivedFrom":makeQuery(id+"F2.opShell","OFFSET_EDGE",EDGE,{"disambiguationData":[OSD([subQ4]),TDD([makeQuery(id+"F1.opExtrude","CAP_EDGE",EDGE,{"disambiguationData":[OSD([subQ4])],"isStart":true})])]})});}
            var Q10;
            {var subQ3=sQuery(id+"F0.wireOp",EDGE,"E0.left");var subQ4=sQuery(id+"F0.wireOp",EDGE,"E0.top");Q10=makeQuery(id+"F16.boolean.opBoolean","SPLIT",EDGE,{"disambiguationData":[TD([makeQuery(id+"F2.opShell","OFFSET_FACE",FACE,{"disambiguationData":[OSD([subQ3])]})])],"derivedFrom":makeQuery(id+"F2.opShell","OFFSET_EDGE",EDGE,{"disambiguationData":[OSD([subQ4]),TDD([makeQuery(id+"F1.opExtrude","CAP_EDGE",EDGE,{"disambiguationData":[OSD([subQ4])],"isStart":false})])]})});}
            chamfer(context, id + "F18", {"entities" : qUnion([Q0, Q1, Q2, Q3, Q4, Q5, Q6, Q7, Q8, Q9, Q10]), "width" : 1 * mm, "tangentPropagation" : true});
        }
        {
            var Q0;
            Q0=makeQuery(id+"F16.opExtrude","CAP_EDGE",EDGE,{"disambiguationData":[OSD([sQuery(id+"F14.wireOp",EDGE,"E70.24")])],"isStart":false});
            var Q1;
            Q1=makeQuery(id+"F16.opExtrude","CAP_EDGE",EDGE,{"disambiguationData":[OSD([sQuery(id+"F14.wireOp",EDGE,"E70.8"),sQuery(id+"F14.wireOp",EDGE,"E70.14")])],"isStart":false});
            var Q2;
            Q2=makeQuery(id+"F16.opExtrude","CAP_EDGE",EDGE,{"disambiguationData":[OSD([sQuery(id+"F14.wireOp",EDGE,"E70.13")])],"isStart":false});
            var Q3;
            Q3=makeQuery(id+"F16.opExtrude","CAP_EDGE",EDGE,{"disambiguationData":[OSD([sQuery(id+"F14.wireOp",EDGE,"E70.11")])],"isStart":false});
            var Q4;
            Q4=makeQuery(id+"F16.opExtrude","CAP_EDGE",EDGE,{"disambiguationData":[OSD([sQuery(id+"F14.wireOp",EDGE,"E70.10")])],"isStart":false});
            var Q5;
            Q5=makeQuery(id+"F16.opExtrude","CAP_EDGE",EDGE,{"disambiguationData":[OSD([sQuery(id+"F14.wireOp",EDGE,"E70.9")])],"isStart":false});
            var Q6;
            Q6=makeQuery(id+"F16.opExtrude","CAP_EDGE",EDGE,{"disambiguationData":[OSD([sQuery(id+"F14.wireOp",EDGE,"E70.12")])],"isStart":false});
            var Q7;
            Q7=makeQuery(id+"F16.opExtrude","CAP_EDGE",EDGE,{"disambiguationData":[OSD([sQuery(id+"F14.wireOp",EDGE,"E70.3")])],"isStart":false});
            var Q8;
            {var subQ1=sQuery(id+"F14.wireOp",EDGE,"E70.2");var subQ5=sQuery(id+"F0.wireOp",EDGE,"E0.top");Q8=makeQuery(id+"F16.boolean.opBoolean","SPLIT",EDGE,{"disambiguationData":[TD([makeQuery(id+"F16.opExtrude","SWEPT_FACE",FACE,{"disambiguationData":[OSD([subQ1])]})])],"derivedFrom":makeQuery(id+"F2.opShell","OFFSET_EDGE",EDGE,{"disambiguationData":[OSD([subQ5]),TDD([makeQuery(id+"F1.opExtrude","CAP_EDGE",EDGE,{"disambiguationData":[OSD([subQ5])],"isStart":false})])]})});}
            var Q9;
            Q9=makeQuery(id+"F16.opExtrude","CAP_EDGE",EDGE,{"disambiguationData":[OSD([sQuery(id+"F14.wireOp",EDGE,"E70.16")])],"isStart":false});
            var Q10;
            Q10=makeQuery(id+"F16.opExtrude","CAP_EDGE",EDGE,{"disambiguationData":[OSD([sQuery(id+"F14.wireOp",EDGE,"E70.18")])],"isStart":false});
            var Q11;
            Q11=makeQuery(id+"F16.opExtrude","CAP_EDGE",EDGE,{"disambiguationData":[OSD([sQuery(id+"F14.wireOp",EDGE,"E70.2")])],"isStart":false});
            var Q12;
            Q12=makeQuery(id+"F16.opExtrude","CAP_EDGE",EDGE,{"disambiguationData":[OSD([sQuery(id+"F14.wireOp",EDGE,"E70.19")])],"isStart":false});
            var Q13;
            Q13=makeQuery(id+"F16.opExtrude","CAP_EDGE",EDGE,{"disambiguationData":[OSD([sQuery(id+"F14.wireOp",EDGE,"E70.4")])],"isStart":false});
            var Q14;
            Q14=makeQuery(id+"F16.opExtrude","CAP_EDGE",EDGE,{"disambiguationData":[OSD([sQuery(id+"F14.wireOp",EDGE,"E70.15")])],"isStart":false});
            var Q15;
            Q15=makeQuery(id+"F16.opExtrude","CAP_EDGE",EDGE,{"disambiguationData":[OSD([sQuery(id+"F14.wireOp",EDGE,"E70.23")])],"isStart":false});
            var Q16;
            Q16=makeQuery(id+"F16.opExtrude","CAP_EDGE",EDGE,{"disambiguationData":[OSD([sQuery(id+"F14.wireOp",EDGE,"E70.22")])],"isStart":false});
            var Q17;
            Q17=makeQuery(id+"F16.opExtrude","CAP_EDGE",EDGE,{"disambiguationData":[OSD([sQuery(id+"F14.wireOp",EDGE,"E70.25")])],"isStart":false});
            var Q18;
            Q18=makeQuery(id+"F16.opExtrude","SWEPT_EDGE",EDGE,{"disambiguationData":[OSD([sQuery(id+"F14.wireOp",EDGE,"E70.15"),sQuery(id+"F14.wireOp",EDGE,"E70.16")])]});
            var Q19;
            Q19=makeQuery(id+"F16.opExtrude","SWEPT_EDGE",EDGE,{"disambiguationData":[OSD([sQuery(id+"F14.wireOp",EDGE,"E70.16"),sQuery(id+"F14.wireOp",EDGE,"E70.19")])]});
            var Q20;
            Q20=makeQuery(id+"F16.opExtrude","SWEPT_EDGE",EDGE,{"disambiguationData":[OSD([sQuery(id+"F14.wireOp",EDGE,"E70.2"),sQuery(id+"F14.wireOp",EDGE,"E70.3")])]});
            var Q21;
            Q21=makeQuery(id+"F16.opExtrude","SWEPT_EDGE",EDGE,{"disambiguationData":[OSD([sQuery(id+"F14.wireOp",EDGE,"E70.3"),sQuery(id+"F14.wireOp",EDGE,"E70.4")])]});
            var Q22;
            Q22=makeQuery(id+"F16.opExtrude","SWEPT_EDGE",EDGE,{"disambiguationData":[OSD([sQuery(id+"F14.wireOp",EDGE,"E70.10"),sQuery(id+"F14.wireOp",EDGE,"E70.13")])]});
            var Q23;
            Q23=makeQuery(id+"F16.opExtrude","SWEPT_EDGE",EDGE,{"disambiguationData":[OSD([sQuery(id+"F14.wireOp",EDGE,"E70.23"),sQuery(id+"F14.wireOp",EDGE,"E70.24")])]});
            fillet(context, id + "F19", {"entities" : qUnion([Q0, Q1, Q2, Q3, Q4, Q5, Q6, Q7, Q8, Q9, Q10, Q11, Q12, Q13, Q14, Q15, Q16, Q17, Q18, Q19, Q20, Q21, Q22, Q23]), "radius" : 1 * mm, "tangentPropagation" : true, "allowEdgeOverflow" : false});
        }
        {
            var Q0;
            Q0=makeQuery(id+"F19.opFillet","SPLIT",FACE,{"disambiguationData":[OD(1.0)],"derivedFrom":makeQuery(id+"F16.opExtrude","CAP_FACE",FACE,{"disambiguationData":[OSD([sQuery(id+"F0.wireOp",EDGE,"E0.bottom"),sQuery(id+"F0.wireOp",EDGE,"E0.right"),sQuery(id+"F14.wireOp",EDGE,"E70.2"),sQuery(id+"F14.wireOp",EDGE,"E70.3"),sQuery(id+"F14.wireOp",EDGE,"E70.4"),sQuery(id+"F14.wireOp",EDGE,"E70.8"),sQuery(id+"F14.wireOp",EDGE,"E70.9"),sQuery(id+"F14.wireOp",EDGE,"E70.10"),sQuery(id+"F14.wireOp",EDGE,"E70.11"),sQuery(id+"F14.wireOp",EDGE,"E70.12"),sQuery(id+"F14.wireOp",EDGE,"E70.13"),sQuery(id+"F14.wireOp",EDGE,"E70.14"),sQuery(id+"F14.wireOp",EDGE,"E70.15"),sQuery(id+"F14.wireOp",EDGE,"E70.16"),sQuery(id+"F14.wireOp",EDGE,"E70.18"),sQuery(id+"F14.wireOp",EDGE,"E70.19"),sQuery(id+"F14.wireOp",EDGE,"E70.22"),sQuery(id+"F14.wireOp",EDGE,"E70.23"),sQuery(id+"F14.wireOp",EDGE,"E70.24"),sQuery(id+"F14.wireOp",EDGE,"E70.25"),sQuery(id+"F14.wireOp",EDGE,"E71.0"),sQuery(id+"F14.wireOp",EDGE,"E71.24"),sQuery(id+"F14.wireOp",EDGE,"E71.26"),sQuery(id+"F14.wireOp",EDGE,"E71.27"),sQuery(id+"F14.wireOp",EDGE,"E71.30"),sQuery(id+"F14.wireOp",EDGE,"E71.32"),sQuery(id+"F14.wireOp",EDGE,"E71.33"),sQuery(id+"F14.wireOp",EDGE,"E71.34"),sQuery(id+"F14.wireOp",EDGE,"E71.35"),sQuery(id+"F14.wireOp",EDGE,"E71.36"),sQuery(id+"F14.wireOp",EDGE,"E71.37"),sQuery(id+"F14.wireOp",EDGE,"E71.38"),sQuery(id+"F14.wireOp",EDGE,"E71.42")])],"isStart":false})});
            var sketch = newSketch(context, id + "F20", { "sketchPlane" : qUnion([Q0])});
            skLineSegment(sketch, "E73", {"start": v(-7.29, -37.09) * mm, "end": v(-7.29, -38.29) * mm, "construction": true});
            skLineSegment(sketch, "E74", {"start": v(-68.25, -18.83) * mm, "end": v(-68.25, -49.19) * mm, "construction": true});
            skCircle(sketch, "E75", {"center": v(-12.73, -1.77) * mm, "radius": 6.35 * mm});
            skLineSegment(sketch, "E76", {"start": v(-17.3, -0.68) * mm, "end": v(-18.54, -1.77) * mm});
            skLineSegment(sketch, "E77", {"start": v(-16.74, -0.18) * mm, "end": v(-16.03, 0.37) * mm});
            skLineSegment(sketch, "E78", {"start": v(-16.03, 0.37) * mm, "end": v(-15.8, 0.07) * mm});
            skLineSegment(sketch, "E79", {"start": v(-15.8, 0.07) * mm, "end": v(-15.34, -0.38) * mm});
            skLineSegment(sketch, "E80", {"start": v(-15.34, -0.38) * mm, "end": v(-14.94, -0.7) * mm});
            skLineSegment(sketch, "E81", {"start": v(-14.94, -0.7) * mm, "end": v(-14.24, -1) * mm});
            skLineSegment(sketch, "E82", {"start": v(-14.24, -1) * mm, "end": v(-13.49, -1.08) * mm});
            skLineSegment(sketch, "E83", {"start": v(-13.49, -1.08) * mm, "end": v(-13.12, -1) * mm});
            skLineSegment(sketch, "E84", {"start": v(-13.12, -1) * mm, "end": v(-12.43, -0.7) * mm});
            skLineSegment(sketch, "E85", {"start": v(-12.43, -0.7) * mm, "end": v(-12.11, -0.5) * mm});
            skLineSegment(sketch, "E86", {"start": v(-12.11, -0.5) * mm, "end": v(-11.82, -0.07) * mm});
            skLineSegment(sketch, "E87", {"start": v(-11.82, -0.07) * mm, "end": v(-11.67, 0.42) * mm});
            skLineSegment(sketch, "E88", {"start": v(-11.67, 0.42) * mm, "end": v(-11.67, 0.8) * mm});
            skLineSegment(sketch, "E89", {"start": v(-11.67, 0.8) * mm, "end": v(-11.86, 1.4) * mm});
            skLineSegment(sketch, "E90", {"start": v(-11.86, 1.4) * mm, "end": v(-12.48, 2.05) * mm});
            skLineSegment(sketch, "E91", {"start": v(-12.48, 2.05) * mm, "end": v(-13.51, 2.5) * mm});
            skLineSegment(sketch, "E92", {"start": v(-13.51, 2.5) * mm, "end": v(-14.4, 2.5) * mm});
            skLineSegment(sketch, "E93", {"start": v(-14.4, 2.5) * mm, "end": v(-15.64, 2.22) * mm});
            skLineSegment(sketch, "E94", {"start": v(-15.64, 2.22) * mm, "end": v(-16.35, 1.92) * mm});
            skLineSegment(sketch, "E95", {"start": v(-16.35, 1.92) * mm, "end": v(-16.9, 1.63) * mm});
            skLineSegment(sketch, "E96", {"start": v(-16.9, 1.63) * mm, "end": v(-17.31, 1.33) * mm});
            skLineSegment(sketch, "E97", {"start": v(-16.74, -0.18) * mm, "end": v(-16.58, -0.39) * mm});
            skLineSegment(sketch, "E98", {"start": v(-16.58, -0.39) * mm, "end": v(-16.22, -0.75) * mm});
            skLineSegment(sketch, "E99", {"start": v(-16.22, -0.75) * mm, "end": v(-15.95, -1.03) * mm});
            skLineSegment(sketch, "E100", {"start": v(-15.95, -1.03) * mm, "end": v(-15.64, -1.24) * mm});
            skLineSegment(sketch, "E101", {"start": v(-15.64, -1.24) * mm, "end": v(-16.27, -1.15) * mm});
            skLineSegment(sketch, "E102", {"start": v(-16.27, -1.15) * mm, "end": v(-16.74, -0.99) * mm});
            skLineSegment(sketch, "E103", {"start": v(-16.74, -0.99) * mm, "end": v(-17.08, -0.85) * mm});
            skLineSegment(sketch, "E104", {"start": v(-17.08, -0.85) * mm, "end": v(-17.3, -0.68) * mm});
            skPoint(sketch, "E105.start.orphan", {"position": v(-19.08, -1.77) * mm});
            skLineSegment(sketch, "E106.MirrorCS", {"start": v(-12.11, -3.04) * mm, "end": v(-11.82, -3.47) * mm});
            skLineSegment(sketch, "E107.MirrorCS", {"start": v(-16.35, -5.46) * mm, "end": v(-16.9, -5.17) * mm});
            skLineSegment(sketch, "E108.MirrorCS", {"start": v(-12.43, -2.84) * mm, "end": v(-12.11, -3.04) * mm});
            skLineSegment(sketch, "E109.MirrorCS", {"start": v(-13.51, -6.05) * mm, "end": v(-14.4, -6.05) * mm});
            skLineSegment(sketch, "E110.MirrorCS", {"start": v(-15.64, -2.3) * mm, "end": v(-16.27, -2.4) * mm});
            skLineSegment(sketch, "E111.MirrorCS", {"start": v(-15.8, -3.61) * mm, "end": v(-15.34, -3.16) * mm});
            skLineSegment(sketch, "E112.MirrorCS", {"start": v(-16.27, -2.4) * mm, "end": v(-16.74, -2.55) * mm});
            skLineSegment(sketch, "E113.MirrorCS", {"start": v(-16.74, -2.55) * mm, "end": v(-17.08, -2.7) * mm});
            skLineSegment(sketch, "E114.MirrorCS", {"start": v(-15.95, -2.51) * mm, "end": v(-15.64, -2.3) * mm});
            skLineSegment(sketch, "E115.MirrorCS", {"start": v(-11.67, -4.34) * mm, "end": v(-11.86, -4.95) * mm});
            skLineSegment(sketch, "E116.MirrorCS", {"start": v(-11.86, -4.95) * mm, "end": v(-12.48, -5.6) * mm});
            skLineSegment(sketch, "E117.MirrorCS", {"start": v(-16.9, -5.17) * mm, "end": v(-17.31, -4.88) * mm});
            skLineSegment(sketch, "E118.MirrorCS", {"start": v(-15.64, -5.76) * mm, "end": v(-16.35, -5.46) * mm});
            skLineSegment(sketch, "E119.MirrorCS", {"start": v(-16.58, -3.15) * mm, "end": v(-16.22, -2.8) * mm});
            skLineSegment(sketch, "E120.MirrorCS", {"start": v(-15.34, -3.16) * mm, "end": v(-14.94, -2.85) * mm});
            skLineSegment(sketch, "E121.MirrorCS", {"start": v(-11.82, -3.47) * mm, "end": v(-11.67, -3.96) * mm});
            skLineSegment(sketch, "E122.MirrorCS", {"start": v(-16.03, -3.91) * mm, "end": v(-15.8, -3.61) * mm});
            skLineSegment(sketch, "E123.MirrorCS", {"start": v(-16.74, -3.36) * mm, "end": v(-16.58, -3.15) * mm});
            skLineSegment(sketch, "E124.MirrorCS", {"start": v(-13.12, -2.53) * mm, "end": v(-12.43, -2.84) * mm});
            skLineSegment(sketch, "E125.MirrorCS", {"start": v(-16.74, -3.36) * mm, "end": v(-16.03, -3.91) * mm});
            skLineSegment(sketch, "E126.MirrorCS", {"start": v(-13.49, -2.46) * mm, "end": v(-13.12, -2.53) * mm});
            skLineSegment(sketch, "E127.MirrorCS", {"start": v(-14.94, -2.85) * mm, "end": v(-14.24, -2.54) * mm});
            skLineSegment(sketch, "E128.MirrorCS", {"start": v(-14.24, -2.54) * mm, "end": v(-13.49, -2.46) * mm});
            skLineSegment(sketch, "E129.MirrorCS", {"start": v(-16.22, -2.8) * mm, "end": v(-15.95, -2.51) * mm});
            skLineSegment(sketch, "E130.MirrorCS", {"start": v(-17.08, -2.7) * mm, "end": v(-17.3, -2.86) * mm});
            skLineSegment(sketch, "E131.MirrorCS", {"start": v(-11.67, -3.96) * mm, "end": v(-11.67, -4.34) * mm});
            skLineSegment(sketch, "E132.MirrorCS", {"start": v(-14.4, -6.05) * mm, "end": v(-15.64, -5.76) * mm});
            skLineSegment(sketch, "E133.MirrorCS", {"start": v(-17.3, -2.86) * mm, "end": v(-18.54, -1.77) * mm});
            skLineSegment(sketch, "E134.MirrorCS", {"start": v(-12.48, -5.6) * mm, "end": v(-13.51, -6.05) * mm});
            skPoint(sketch, "E135.MirrorP", {"position": v(-20.6, -3.3) * mm});
            skArc(sketch, "E136", {"start": v(-17.31, -4.88) * mm, "mid": v(-7.2, -1.77) * mm, "end": v(-17.31, 1.33) * mm});
            skText(sketch, "E137", { "text": "E-Wing", "fontName": "NotoSans-Bold.ttf"});
            skLineSegment(sketch, "E138", {"start": v(-10.65, 5.83) * mm, "end": v(-10.65, 4.23) * mm, "construction": true});
            skLineSegment(sketch, "E139", {"start": v(-13.28, -10.1) * mm, "end": v(-13.67, -8.55) * mm, "construction": true});
            skLineSegment(sketch, "E140", {"start": v(-13.67, -8.55) * mm, "end": v(-2.63, -5.79) * mm, "construction": true});
            skPoint(sketch, "E141.0", {"position": v(-26.67, -19.05) * mm});
            skLineSegment(sketch, "E142", {"start": v(-26.67, -19.05) * mm, "end": v(-26.67, -18.05) * mm, "construction": true});
            skLineSegment(sketch, "E143", {"start": v(-26.67, -18.05) * mm, "end": v(-25.67, -18.05) * mm, "construction": true});
            const initialGuessF20  = {"E137": [-0.02044, -0.01805, 0, 1, 0.00523]};
            skSetInitialGuess(sketch, initialGuessF20);
            skSolve(sketch);
        }
        {
            var Q0;
            Q0=qSketchRegion(id+"F20",true);
            extrude(context, id + "F21", {"entities" : qUnion([Q0]), "operationType" : NewBodyOperationType.REMOVE, "oppositeDirection" : true, "depth" : 1 * mm, "offsetDistance" : 25 * mm});
        }
    });
